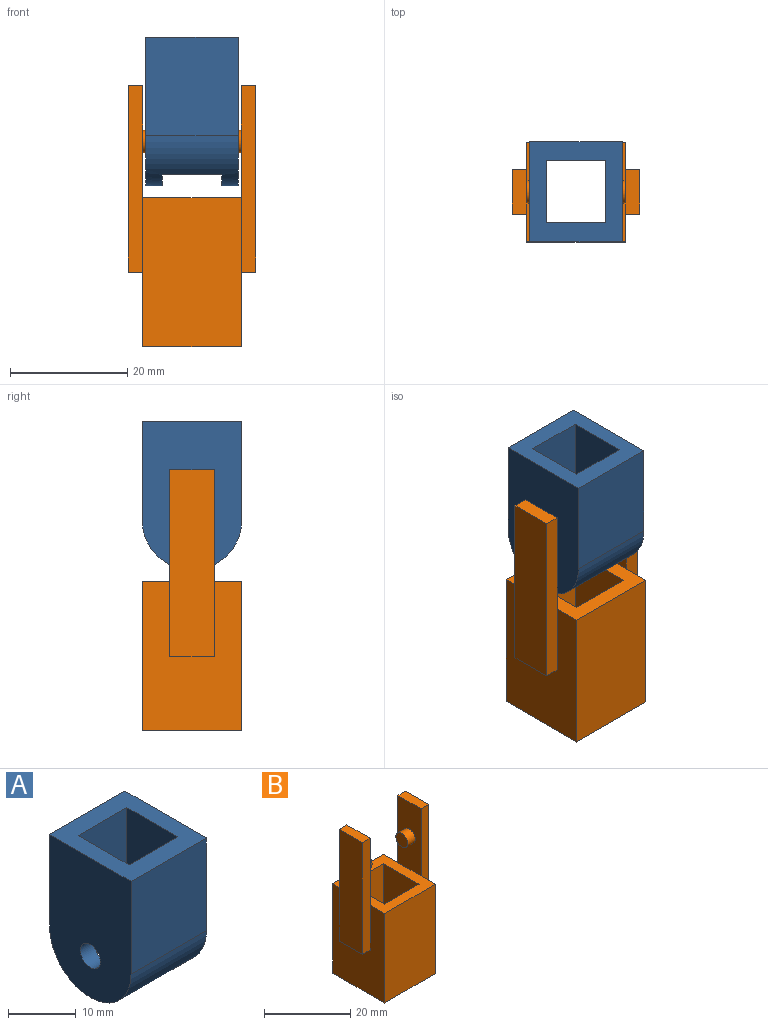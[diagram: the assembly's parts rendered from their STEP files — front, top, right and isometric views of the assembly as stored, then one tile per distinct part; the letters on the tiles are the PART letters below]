
ASSEMBLY  parts=2 mates=1
PART A: 12 faces, bbox 15.7x17x25.3 mm
  f0: plane 23.42x10.16mm, normal (0,-1,0), area 237.9mm2, adj f1,f7,f8,f11
  f1: plane 25.27x10.61mm, normal (-1,0,0), area 248.1mm2, adj f0,f2,f8,f10,f11
  f2: plane 23.42x10.16mm, normal (0,1,0), area 237.9mm2, adj f1,f7,f8,f11
  f3: plane 25.27x17.02mm, normal (1,0,0), area 385.2mm2, adj f4,f6,f8,f10,f11
  f4: plane 16.76x15.75mm, normal (0,1,0), area 264mm2, adj f3,f5,f8,f11
  f5: plane 25.27x17.02mm, normal (-1,0,0), area 385.2mm2, adj f4,f6,f8,f9,f11
  f6: plane 16.76x15.75mm, normal (0,-1,0), area 264mm2, adj f3,f5,f8,f11
  f7: plane 25.27x10.61mm, normal (1,0,0), area 248.1mm2, adj f0,f2,f8,f9,f11
  f8: plane 17.02x15.75mm, normal (0,0,1), area 160.2mm2, adj f0,f1,f2,f3,f4,f5,f6,f7
  f9: cylinder r=2.1mm len=4.19mm, axis (1,0,0), area 36.8mm2, adj f5,f7
  f10: cylinder r=2.1mm len=4.19mm, axis (1,0,0), area 36.8mm2, adj f1,f3
  f11: cylinder r=8.51mm len=17.02mm, axis (1,0,0), area 304.6mm2, adj f0,f1,f2,f3,f4,f5,f6,f7
PART B: 26 faces, bbox 21.8x17x44.5 mm
  f0: plane 25.4x11.34mm, normal (0,-1,0), area 288.2mm2, adj f1,f7,f8,f9
  f1: plane 25.4x11.64mm, normal (-1,0,0), area 295.7mm2, adj f0,f2,f8,f9
  f2: plane 25.4x11.34mm, normal (0,1,0), area 288.2mm2, adj f1,f7,f8,f9
  f3: plane 25.4x17.02mm, normal (1,0,0), area 335.5mm2, adj f4,f6,f8,f9,f19,f21,f22
  f4: plane 25.4x16.72mm, normal (0,1,0), area 424.7mm2, adj f3,f5,f8,f9
  f5: plane 25.4x17.02mm, normal (-1,0,0), area 335.5mm2, adj f4,f6,f8,f9,f10,f11,f12
  f6: plane 25.4x16.72mm, normal (0,-1,0), area 424.7mm2, adj f3,f5,f8,f9
  f7: plane 25.4x11.64mm, normal (1,0,0), area 295.7mm2, adj f0,f2,f8,f9
  f8: plane 17.02x16.72mm, normal (0,0,1), area 152.4mm2, adj f0,f1,f2,f3,f4,f5,f6,f7
  f9: plane 17.02x16.72mm, normal (0,0,-1), area 152.4mm2, adj f0,f1,f2,f3,f4,f5,f6,f7
  f10: plane 31.75x2.54mm, normal (0,1,0), area 80.6mm2, adj f5,f11,f13,f14,f15
  f11: plane 7.62x2.54mm, normal (0,0,-1), area 19.4mm2, adj f5,f10,f12,f14
  f12: plane 31.75x2.54mm, normal (0,-1,0), area 80.6mm2, adj f5,f11,f13,f14,f15
  f13: plane 7.62x2.54mm, normal (0,0,1), area 19.4mm2, adj f10,f12,f14,f15
  f14: plane 31.75x7.62mm, normal (-1,0,0), area 241.9mm2, adj f10,f11,f12,f13
  f15: plane 19.05x7.62mm, normal (1,0,0), area 133.8mm2, adj f8,f10,f12,f13,f16
  f16: cylinder r=1.91mm len=3.81mm, axis (-1,0,0), area 30.4mm2, adj f15,f17
  f17: plane 3.81x3.81mm, normal (1,0,0), area 11.4mm2, adj f16
  f18: plane 19.05x7.62mm, normal (-1,0,0), area 133.8mm2, adj f8,f19,f20,f21,f24
  f19: plane 31.75x2.54mm, normal (0,1,0), area 80.6mm2, adj f3,f18,f20,f22,f23
  f20: plane 7.62x2.54mm, normal (0,0,1), area 19.4mm2, adj f18,f19,f21,f23
  f21: plane 31.75x2.54mm, normal (0,-1,0), area 80.6mm2, adj f3,f18,f20,f22,f23
  f22: plane 7.62x2.54mm, normal (0,0,-1), area 19.4mm2, adj f3,f19,f21,f23
  f23: plane 31.75x7.62mm, normal (1,0,0), area 241.9mm2, adj f19,f20,f21,f22
  f24: cylinder r=1.91mm len=3.81mm, axis (1,0,0), area 30.4mm2, adj f18,f25
  f25: plane 3.81x3.81mm, normal (-1,0,0), area 11.4mm2, adj f24
PLACE A t=(0,0,27.28)mm
PLACE B at identity fixed
MATE revolute A.f9 <-> B.f16  axis (-1,0,0) through (-7.88,0,34.93)mm
